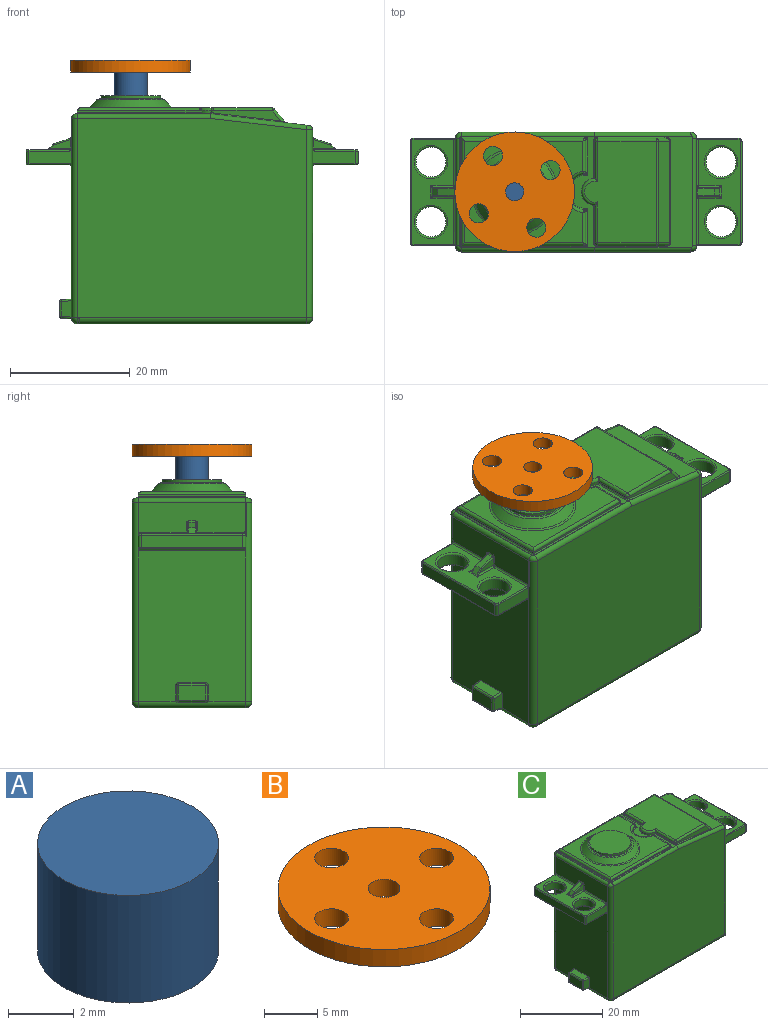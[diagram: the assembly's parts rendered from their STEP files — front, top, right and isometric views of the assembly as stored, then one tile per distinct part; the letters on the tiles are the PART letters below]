
ASSEMBLY  parts=3 mates=4
PART A: 3 faces, bbox 5.5x5.5x4 mm
  f0: cylinder r=2.75mm len=5.5mm, axis (0,0,1), area 69.1mm2, adj f1,f2
  f1: plane 5.5x5.5mm, normal (0,0,-1), area 23.8mm2, adj f0
  f2: plane 5.5x5.5mm, normal (0,0,1), area 23.8mm2, adj f0
PART B: 8 faces, bbox 20x20x2 mm
  f0: cylinder r=1.5mm len=3mm, axis (0,0,-1), area 18.8mm2, adj f2,f3
  f1: cylinder r=10mm len=20mm, axis (0,0,-1), area 125.7mm2, adj f2,f3
  f2: plane 20x20mm, normal (0,0,1), area 274.9mm2, adj f0,f1,f4,f5,f6,f7
  f3: plane 20x20mm, normal (0,0,-1), area 274.9mm2, adj f0,f1,f4,f5,f6,f7
  f4: cylinder r=1.6mm len=3.2mm, axis (0,0,1), area 20.1mm2, adj f2,f3
  f5: cylinder r=1.6mm len=3.2mm, axis (0,0,1), area 20.1mm2, adj f2,f3
  f6: cylinder r=1.6mm len=3.2mm, axis (0,0,1), area 20.1mm2, adj f2,f3
  f7: cylinder r=1.6mm len=3.2mm, axis (0,0,1), area 20.1mm2, adj f2,f3
PART C: 234 faces, bbox 55.8x20.2x38.3 mm
  f0: torus R=2.8mm, axis (0,0,1), area 7.7mm2, adj f17,f31
  f1: torus R=2.8mm, axis (0,0,1), area 7.7mm2, adj f18,f31
  f2: torus R=2.8mm, axis (0,0,1), area 7.7mm2, adj f18,f21
  f3: torus R=2.8mm, axis (0,0,1), area 7.7mm2, adj f17,f21
  f4: torus R=2.8mm, axis (0,0,1), area 7.7mm2, adj f15,f22
  f5: torus R=2.8mm, axis (0,0,1), area 7.7mm2, adj f16,f22
  f6: torus R=2.8mm, axis (0,0,1), area 7.7mm2, adj f16,f20
  f7: torus R=2.8mm, axis (0,0,1), area 7.7mm2, adj f15,f20
  f8: torus R=7.21mm, axis (0,0,1), area 17.3mm2, adj f11,f114
  f9: torus R=5.29mm, axis (0,0,-1), area 13.5mm2, adj f11,f121
  f10: cylinder r=5mm len=10mm, axis (0,0,1), area 15.7mm2, adj f121,f122
  f11: cone r=5.5mm half-angle=45deg, axis (0,0,-1), area 67mm2, adj f8,f9
  f12: cylinder r=2.25mm len=4.5mm, axis (0,0,-1), area 3.5mm2, adj f66,f89,f90,f105,f196,f205
  f13: cylinder r=1mm len=33.35mm, axis (0,0,-1), area 52.4mm2, adj f23,f30,f39,f48,f67,f77,f165,f173
  f14: cylinder r=1mm len=33.35mm, axis (0,0,-1), area 52.5mm2, adj f25,f26,f39,f47,f67,f73,f159,f179
  f15: cylinder r=2.5mm len=5mm, axis (0,0,-1), area 29.8mm2, adj f4,f7
  f16: cylinder r=2.5mm len=5mm, axis (0,0,-1), area 29.8mm2, adj f5,f6
  f17: cylinder r=2.5mm len=5mm, axis (0,0,-1), area 29.8mm2, adj f0,f3
  f18: cylinder r=2.5mm len=5mm, axis (0,0,-1), area 29.8mm2, adj f1,f2
  f19: plane 18.3x0.05mm, normal (0,0,1), area 0.9mm2, adj f73,f75,f77,f131
  f20: plane 17.6x7.1mm, normal (0,0,1), area 67.6mm2, adj f6,f7,f154,f155,f156,f157,f158,f160
  f21: plane 17.6x7.1mm, normal (0,0,-1), area 75.7mm2, adj f2,f3,f145,f167,f168,f170,f171,f172
  f22: plane 17.6x7.1mm, normal (0,0,-1), area 75.7mm2, adj f4,f5,f152,f174,f175,f176,f177,f178
  f23: plane 7.1x2.3mm, normal (0,-1,0), area 14.9mm2, adj f13,f35,f164,f165,f173,f174
  f24: plane 17x2.1mm, normal (-1,0,0), area 35.7mm2, adj f34,f35,f162,f176
  f25: plane 7.1x2.3mm, normal (0,1,0), area 14.9mm2, adj f14,f34,f159,f160,f178,f179
  f26: plane 38.3x33.35mm, normal (0,1,0), area 1262.2mm2, adj f14,f33,f43,f70,f71
  f27: plane 7.1x2.3mm, normal (0,1,0), area 14.9mm2, adj f33,f36,f166,f167,f185,f186
  f28: plane 17x2.1mm, normal (1,0,0), area 35.7mm2, adj f36,f37,f170,f183
  f29: plane 7.1x2.3mm, normal (0,-1,0), area 14.9mm2, adj f32,f37,f169,f171,f180,f181
  f30: plane 38.3x33.35mm, normal (0,-1,0), area 1262.2mm2, adj f13,f32,f42,f78,f79
  f31: plane 17.6x7.1mm, normal (0,0,1), area 67.6mm2, adj f0,f1,f147,f148,f149,f150,f151,f181
  f32: cylinder r=1mm len=31.46mm, axis (0,0,-1), area 49.5mm2, adj f29,f30,f38,f45,f68,f76,f169,f180
  f33: cylinder r=1mm len=31.46mm, axis (0,0,-1), area 49.5mm2, adj f26,f27,f38,f46,f68,f72,f166,f186
  f34: cylinder r=0.5mm len=2.1mm, axis (0,0,-1), area 1.6mm2, adj f24,f25,f161,f177
  f35: cylinder r=0.5mm len=2.1mm, axis (0,0,-1), area 1.6mm2, adj f23,f24,f163,f175
  f36: cylinder r=0.5mm len=2.1mm, axis (0,0,-1), area 1.6mm2, adj f27,f28,f168,f184
  f37: cylinder r=0.5mm len=2.1mm, axis (0,0,-1), area 1.6mm2, adj f28,f29,f172,f182
  f38: plane 25.38x18.08mm, normal (1,0,0), area 455.3mm2, adj f32,f33,f41,f145,f166,f169
  f39: plane 25.38x18.08mm, normal (-1,0,0), area 438.4mm2, adj f13,f14,f44,f50,f52,f53,f54,f55
  f40: plane 38.3x18mm, normal (0,0,-1), area 689.4mm2, adj f41,f42,f43,f44
  f41: cylinder r=1mm len=18mm, axis (0,-1,0), area 28.3mm2, adj f38,f40,f45,f46
  f42: cylinder r=1mm len=38.3mm, axis (-1,0,0), area 60.2mm2, adj f30,f40,f45,f48
  f43: cylinder r=1mm len=38.3mm, axis (1,0,0), area 60.2mm2, adj f26,f40,f46,f47
  f44: cylinder r=1mm len=18mm, axis (0,1,0), area 27.4mm2, adj f39,f40,f47,f48,f51,f60,f61
  f45: sphere r=1mm, area 1.6mm2, adj f32,f41,f42
  f46: sphere r=1mm, area 1mm2, adj f33,f41,f43
  f47: sphere r=1mm, area 1.6mm2, adj f14,f43,f44
  f48: sphere r=1mm, area 2.1mm2, adj f13,f42,f44
  f49: plane 4.45x2.45mm, normal (-1,0,0), area 10.9mm2, adj f56,f59,f62,f65
  f50: plane 2.75x1.73mm, normal (-0.09,1,0), area 4.5mm2, adj f39,f55,f61,f62
  f51: plane 4.76x1.74mm, normal (-0.09,0,-1), area 8mm2, adj f44,f60,f61,f65
  f52: plane 2.75x1.73mm, normal (-0.09,-1,0), area 4.5mm2, adj f39,f54,f59,f60
  f53: plane 4.75x1.73mm, normal (-0.09,0,1), area 8mm2, adj f39,f54,f55,f56
  f54: cylinder r=0.3mm len=1.74mm, axis (0.99,-0.09,0.09), area 0.8mm2, adj f39,f52,f53,f57
  f55: cylinder r=0.3mm len=1.74mm, axis (0.99,0.09,0.09), area 0.8mm2, adj f39,f50,f53,f58
  f56: cylinder r=0.3mm len=4.45mm, axis (0,-1,0), area 2mm2, adj f49,f53,f57,f58
  f57: sphere r=0.3mm, area 0.1mm2, adj f54,f56,f59
  f58: sphere r=0.3mm, area 0.1mm2, adj f55,f56,f62
  f59: cylinder r=0.3mm len=2.45mm, axis (0,0,-1), area 1.1mm2, adj f49,f52,f57,f63
  f60: cylinder r=0.3mm len=1.75mm, axis (0.99,-0.09,-0.09), area 0.8mm2, adj f39,f44,f51,f52,f63
  f61: cylinder r=0.3mm len=1.75mm, axis (0.99,0.09,-0.09), area 0.8mm2, adj f39,f44,f50,f51,f64
  f62: cylinder r=0.3mm len=2.45mm, axis (0,0,1), area 1.1mm2, adj f49,f50,f58,f64
  f63: sphere r=0.3mm, area 0.1mm2, adj f59,f60,f65
  f64: sphere r=0.3mm, area 0.1mm2, adj f61,f62,f65
  f65: cylinder r=0.3mm len=4.45mm, axis (0,1,0), area 2mm2, adj f49,f51,f63,f64
  f66: plane 22.46x18.5mm, normal (0,0,1), area 29mm2, adj f12,f69,f71,f73,f77,f79,f123,f125
  f67: plane 18.2x5.15mm, normal (-1,0,0), area 85.5mm2, adj f13,f14,f75,f153,f154,f156,f159,f165
  f68: plane 18.2x3.23mm, normal (1,0,0), area 51mm2, adj f32,f33,f74,f146,f147,f149,f180,f186
  f69: plane 18.53x16.37mm, normal (0.12,0,0.99), area 70.4mm2, adj f66,f70,f72,f74,f76,f78,f198,f199
  f70: cylinder r=0.75mm len=16.18mm, axis (0.99,0,-0.12), area 19.1mm2, adj f26,f69,f71,f72
  f71: cylinder r=0.75mm len=22.3mm, axis (-1,0,0), area 26.2mm2, adj f26,f66,f70,f73
  f72: bspline ~1x1mm, area 1.3mm2, adj f33,f69,f70,f74
  f73: torus R=0.25mm, axis (0,0,1), area 1.3mm2, adj f14,f19,f66,f71,f75,f124,f127
  f74: cylinder r=0.75mm len=18mm, axis (0,1,0), area 19.6mm2, adj f68,f69,f72,f76
  f75: cylinder r=0.75mm len=18mm, axis (0,-1,0), area 21.2mm2, adj f19,f67,f73,f77
  f76: bspline ~1x1mm, area 1.3mm2, adj f32,f69,f74,f78
  f77: torus R=0.25mm, axis (0,0,1), area 1.3mm2, adj f13,f19,f66,f75,f79,f130,f132
  f78: cylinder r=0.75mm len=16.18mm, axis (-0.99,0,0.12), area 19.1mm2, adj f30,f69,f76,f79
  f79: cylinder r=0.75mm len=22.3mm, axis (1,0,0), area 26.2mm2, adj f30,f66,f77,f78
  f80: plane 2.8x1.1mm, normal (-0.32,0,0.95), area 3.2mm2, adj f83,f153,f220,f230
  f81: plane 3.22x1.42mm, normal (0,-1,0), area 2.8mm2, adj f155,f218,f220,f223
  f82: plane 3.22x1.42mm, normal (0,1,0), area 2.8mm2, adj f158,f228,f230,f232
  f83: plane 1.4x0.92mm, normal (-0.71,0,0.71), area 1.5mm2, adj f80,f157,f217,f218,f226,f228
  f84: plane 2.8x1.1mm, normal (0.32,0,0.95), area 3.2mm2, adj f87,f146,f191,f212
  f85: plane 3.22x1.42mm, normal (0,-1,0), area 2.8mm2, adj f148,f210,f212,f214
  f86: plane 3.22x1.42mm, normal (0,1,0), area 2.8mm2, adj f151,f189,f191,f194
  f87: plane 1.4x0.92mm, normal (0.71,0,0.71), area 1.5mm2, adj f84,f150,f188,f189,f208,f210
  f88: plane 11.16x1.67mm, normal (0,1,0), area 10.1mm2, adj f94,f95,f101,f203
  f89: plane 6.25x0.3mm, normal (-1,0,0), area 1.9mm2, adj f12,f95,f104,f205
  f90: plane 6.25x0.3mm, normal (-1,0,0), area 1.9mm2, adj f12,f96,f106,f196
  f91: plane 11.16x1.67mm, normal (0,-1,0), area 10.1mm2, adj f93,f96,f98,f199
  f92: plane 17x2.24mm, normal (0.77,0,0.64), area 49.5mm2, adj f93,f94,f100,f201
  f93: cylinder r=0.5mm len=2.56mm, axis (0.64,0,-0.77), area 2mm2, adj f91,f92,f99,f200
  f94: cylinder r=0.5mm len=2.56mm, axis (-0.64,0,0.77), area 2mm2, adj f88,f92,f102,f202
  f95: cylinder r=0.5mm len=0.5mm, axis (0,0,-1), area 0.2mm2, adj f88,f89,f103,f204,f206
  f96: cylinder r=0.5mm len=0.5mm, axis (0,0,-1), area 0.2mm2, adj f90,f91,f107,f197,f198
  f97: plane 17x12.02mm, normal (0,0,1), area 172.6mm2, adj f98,f100,f101,f104,f105,f106
  f98: cylinder r=0.5mm len=9.77mm, axis (-1,0,0), area 7.7mm2, adj f91,f97,f99,f107
  f99: sphere r=0.5mm, area 0.2mm2, adj f93,f98,f100
  f100: cylinder r=0.5mm len=17mm, axis (0,1,0), area 7.4mm2, adj f92,f97,f99,f102
  f101: cylinder r=0.5mm len=9.77mm, axis (1,0,0), area 7.7mm2, adj f88,f97,f102,f103
  f102: sphere r=0.5mm, area 0.2mm2, adj f94,f100,f101
  f103: sphere r=0.5mm, area 0.2mm2, adj f95,f101,f104
  f104: cylinder r=0.5mm len=6.82mm, axis (0,1,0), area 5.1mm2, adj f89,f97,f103,f105
  f105: torus R=1.75mm, axis (0,0,1), area 5.6mm2, adj f12,f97,f104,f106
  f106: cylinder r=0.5mm len=6.82mm, axis (0,1,0), area 5.1mm2, adj f90,f97,f105,f107
  f107: sphere r=0.5mm, area 0.4mm2, adj f96,f98,f106
  f108: plane 20.5x0.3mm, normal (0,-1,0), area 6.2mm2, adj f109,f117,f129,f134
  f109: plane 18x0.3mm, normal (-1,0,0), area 5.4mm2, adj f108,f110,f115,f131
  f110: plane 20.5x0.3mm, normal (0,1,0), area 6.2mm2, adj f109,f116,f128,f137
  f111: plane 5.41x0.3mm, normal (1,0,0), area 1.6mm2, adj f118,f125,f137,f144
  f112: cylinder r=3mm len=5.98mm, axis (0,0,1), area 2.7mm2, adj f120,f123,f141,f144
  f113: plane 5.41x0.3mm, normal (1,0,0), area 1.6mm2, adj f119,f126,f134,f141
  f114: plane 19.8x17mm, normal (0,0,1), area 157.7mm2, adj f8,f115,f116,f117,f118,f119,f120
  f115: cylinder r=0.5mm len=18mm, axis (0,-1,0), area 13.7mm2, adj f109,f114,f116,f117
  f116: cylinder r=0.5mm len=20.5mm, axis (-1,0,0), area 15.8mm2, adj f110,f114,f115,f138
  f117: cylinder r=0.5mm len=20.5mm, axis (1,0,0), area 15.8mm2, adj f108,f114,f115,f133
  f118: cylinder r=0.5mm len=5.41mm, axis (0,1,0), area 4.1mm2, adj f111,f114,f138,f143
  f119: cylinder r=0.5mm len=5.41mm, axis (0,1,0), area 4.1mm2, adj f113,f114,f133,f140
  f120: torus R=3.5mm, axis (0,0,1), area 7.3mm2, adj f112,f114,f140,f143
  f121: plane 10.59x10.59mm, normal (0,0,1), area 9.5mm2, adj f9,f10
  f122: plane 10x10mm, normal (0,0,1), area 78.5mm2, adj f10
  f123: torus R=2.8mm, axis (0,0,1), area 2.9mm2, adj f66,f112,f139,f142
  f124: cylinder r=0.18mm len=0.05mm, axis (1,-0.09,0.02), area 0mm2, adj f73,f127,f128
  f125: cylinder r=0.2mm len=6.41mm, axis (0,-1,0), area 1.9mm2, adj f66,f111,f136,f142
  f126: cylinder r=0.2mm len=6.41mm, axis (0,-1,0), area 1.9mm2, adj f66,f113,f135,f139
  f127: cylinder r=0.18mm len=0.05mm, axis (-0.08,-1,0), area 0mm2, adj f73,f124,f131
  f128: cylinder r=0.2mm len=21.15mm, axis (1,0,0), area 6.5mm2, adj f66,f110,f124,f131,f136
  f129: cylinder r=0.2mm len=21.15mm, axis (-1,0,0), area 6.5mm2, adj f66,f108,f130,f131,f135
  f130: cylinder r=0.18mm len=0.05mm, axis (1,-0.08,0), area 0mm2, adj f77,f129,f132
  f131: cylinder r=0.2mm len=18.3mm, axis (0,1,0), area 5.7mm2, adj f19,f109,f127,f128,f129,f132
  f132: cylinder r=0.18mm len=0.05mm, axis (0.09,1,0.02), area 0mm2, adj f77,f130,f131
  f133: bspline ~0.5x0.5mm, area 0.2mm2, adj f117,f119,f134
  f134: cylinder r=0.3mm len=0.3mm, axis (0,0,1), area 0.1mm2, adj f108,f113,f133,f135
  f135: bspline ~0.5x0.5mm, area 0.1mm2, adj f126,f129,f134
  f136: bspline ~0.5x0.5mm, area 0.1mm2, adj f125,f128,f137
  f137: cylinder r=0.3mm len=0.3mm, axis (0,0,1), area 0.1mm2, adj f110,f111,f136,f138
  f138: bspline ~0.5x0.5mm, area 0.2mm2, adj f116,f118,f137
  f139: bspline ~0.49x0.47mm, area 0.1mm2, adj f123,f126,f141
  f140: bspline ~0.5x0.5mm, area 0.2mm2, adj f119,f120,f141
  f141: cylinder r=0.3mm len=0.3mm, axis (0,0,1), area 0.1mm2, adj f112,f113,f139,f140
  f142: bspline ~0.49x0.47mm, area 0.1mm2, adj f123,f125,f144
  f143: bspline ~0.5x0.5mm, area 0.2mm2, adj f118,f120,f144
  f144: cylinder r=0.3mm len=0.3mm, axis (0,0,1), area 0.1mm2, adj f111,f112,f142,f143
  f145: cylinder r=0.3mm len=17.6mm, axis (0,-1,0), area 8.3mm2, adj f21,f38,f166,f169
  f146: cylinder r=0.3mm len=1.1mm, axis (0,1,0), area 0.4mm2, adj f68,f84,f190,f209
  f147: cylinder r=0.3mm len=7.85mm, axis (0,-1,0), area 3.7mm2, adj f31,f68,f180,f215
  f148: cylinder r=0.3mm len=3.92mm, axis (-1,0,0), area 1.7mm2, adj f31,f85,f207,f208,f215
  f149: cylinder r=0.3mm len=7.85mm, axis (0,-1,0), area 3.7mm2, adj f31,f68,f186,f195
  f150: cylinder r=0.3mm len=2.1mm, axis (0,1,0), area 0.4mm2, adj f31,f87,f187,f207
  f151: cylinder r=0.3mm len=3.92mm, axis (1,0,0), area 1.7mm2, adj f31,f86,f187,f188,f195
  f152: cylinder r=0.3mm len=17.6mm, axis (0,1,0), area 8.3mm2, adj f22,f39,f173,f179
  f153: cylinder r=0.3mm len=1.1mm, axis (0,-1,0), area 0.4mm2, adj f67,f80,f219,f227
  f154: cylinder r=0.3mm len=7.85mm, axis (0,1,0), area 3.7mm2, adj f20,f67,f165,f224
  f155: cylinder r=0.3mm len=3.92mm, axis (-1,0,0), area 1.7mm2, adj f20,f81,f216,f217,f224
  f156: cylinder r=0.3mm len=7.85mm, axis (0,1,0), area 3.7mm2, adj f20,f67,f159,f233
  f157: cylinder r=0.3mm len=2.1mm, axis (0,1,0), area 0.4mm2, adj f20,f83,f216,f225
  f158: cylinder r=0.3mm len=3.92mm, axis (1,0,0), area 1.7mm2, adj f20,f82,f225,f226,f233
  f159: torus R=0.5mm, axis (0,1,0), area 0.1mm2, adj f14,f25,f67,f156,f160
  f160: cylinder r=0.2mm len=6.8mm, axis (1,0,0), area 2.1mm2, adj f20,f25,f159,f161
  f161: torus R=0.3mm, axis (0,0,1), area 0.2mm2, adj f20,f34,f160,f162
  f162: cylinder r=0.2mm len=17mm, axis (0,1,0), area 5.3mm2, adj f20,f24,f161,f163
  f163: torus R=0.3mm, axis (0,0,1), area 0.2mm2, adj f20,f35,f162,f164
  f164: cylinder r=0.2mm len=6.8mm, axis (-1,0,0), area 2.1mm2, adj f20,f23,f163,f165
  f165: torus R=0.5mm, axis (0,-1,0), area 0.1mm2, adj f13,f23,f67,f154,f164
  f166: torus R=0.5mm, axis (0,1,0), area 0.1mm2, adj f27,f33,f38,f145,f167
  f167: cylinder r=0.2mm len=6.8mm, axis (-1,0,0), area 2.1mm2, adj f21,f27,f166,f168
  f168: torus R=0.3mm, axis (0,0,1), area 0.2mm2, adj f21,f36,f167,f170
  f169: torus R=0.5mm, axis (0,-1,0), area 0.1mm2, adj f29,f32,f38,f145,f171
  f170: cylinder r=0.2mm len=17mm, axis (0,1,0), area 5.3mm2, adj f21,f28,f168,f172
  f171: cylinder r=0.2mm len=6.8mm, axis (1,0,0), area 2.1mm2, adj f21,f29,f169,f172
  f172: torus R=0.3mm, axis (0,0,1), area 0.2mm2, adj f21,f37,f170,f171
  f173: torus R=0.5mm, axis (0,-1,0), area 0.1mm2, adj f13,f23,f39,f152,f174
  f174: cylinder r=0.2mm len=6.8mm, axis (1,0,0), area 2.1mm2, adj f22,f23,f173,f175
  f175: torus R=0.3mm, axis (0,0,1), area 0.2mm2, adj f22,f35,f174,f176
  f176: cylinder r=0.2mm len=17mm, axis (0,-1,0), area 5.3mm2, adj f22,f24,f175,f177
  f177: torus R=0.3mm, axis (0,0,1), area 0.2mm2, adj f22,f34,f176,f178
  f178: cylinder r=0.2mm len=6.8mm, axis (-1,0,0), area 2.1mm2, adj f22,f25,f177,f179
  f179: torus R=0.5mm, axis (0,1,0), area 0.1mm2, adj f14,f25,f39,f152,f178
  f180: torus R=0.5mm, axis (0,-1,0), area 0.1mm2, adj f29,f32,f68,f147,f181
  f181: cylinder r=0.2mm len=6.8mm, axis (-1,0,0), area 2.1mm2, adj f29,f31,f180,f182
  f182: torus R=0.3mm, axis (0,0,1), area 0.2mm2, adj f31,f37,f181,f183
  f183: cylinder r=0.2mm len=17mm, axis (0,-1,0), area 5.3mm2, adj f28,f31,f182,f184
  f184: torus R=0.3mm, axis (0,0,1), area 0.2mm2, adj f31,f36,f183,f185
  f185: cylinder r=0.2mm len=6.8mm, axis (1,0,0), area 2.1mm2, adj f27,f31,f184,f186
  f186: torus R=0.5mm, axis (0,1,0), area 0.1mm2, adj f27,f33,f68,f149,f185
  f187: bspline ~0.35x0.35mm, area 0mm2, adj f150,f151,f188
  f188: bspline ~0.5x0.35mm, area 0.1mm2, adj f87,f151,f187,f189
  f189: cylinder r=0.2mm len=0.7mm, axis (-0.71,0,0.71), area 0.2mm2, adj f86,f87,f188,f191
  f190: torus R=0.5mm, axis (0,-1,0), area 0mm2, adj f146,f191,f192
  f191: cylinder r=0.2mm len=2.86mm, axis (-0.95,0,0.32), area 0.9mm2, adj f84,f86,f189,f190,f193
  f192: bspline ~0.39x0.36mm, area 0mm2, adj f68,f190,f193
  f193: bspline ~0.22x0.2mm, area 0mm2, adj f68,f191,f192,f194
  f194: cylinder r=0.2mm len=1.42mm, axis (0,0,-1), area 0.4mm2, adj f68,f86,f193,f195
  f195: bspline ~0.3x0.3mm, area 0.1mm2, adj f149,f151,f194
  f196: cylinder r=0.2mm len=6.26mm, axis (0,-1,0), area 2mm2, adj f12,f66,f90,f197
  f197: torus R=0.7mm, axis (0,0,1), area 0.1mm2, adj f66,f96,f196,f198
  f198: bspline ~0.51x0.34mm, area 0.1mm2, adj f66,f69,f96,f197,f199
  f199: cylinder r=0.2mm len=11.18mm, axis (-0.99,0,0.12), area 3.5mm2, adj f69,f91,f198,f200
  f200: bspline ~1.01x0.7mm, area 0.3mm2, adj f69,f93,f199,f201
  f201: cylinder r=0.2mm len=17mm, axis (0,-1,0), area 2.6mm2, adj f69,f92,f200,f202
  f202: bspline ~1.01x0.7mm, area 0.3mm2, adj f69,f94,f201,f203
  f203: cylinder r=0.2mm len=11.18mm, axis (0.99,0,-0.12), area 3.5mm2, adj f69,f88,f202,f204
  f204: bspline ~0.51x0.34mm, area 0.1mm2, adj f66,f69,f95,f203,f206
  f205: cylinder r=0.2mm len=6.26mm, axis (0,-1,0), area 2mm2, adj f12,f66,f89,f206
  f206: torus R=0.7mm, axis (0,0,1), area 0.1mm2, adj f66,f95,f204,f205
  f207: bspline ~0.35x0.35mm, area 0mm2, adj f148,f150,f208
  f208: bspline ~0.5x0.35mm, area 0.1mm2, adj f87,f148,f207,f210
  f209: torus R=0.5mm, axis (0,-1,0), area 0mm2, adj f146,f211,f212
  f210: cylinder r=0.2mm len=0.7mm, axis (0.71,0,-0.71), area 0.2mm2, adj f85,f87,f208,f212
  f211: bspline ~0.39x0.36mm, area 0mm2, adj f68,f209,f213
  f212: cylinder r=0.2mm len=2.86mm, axis (0.95,0,-0.32), area 0.9mm2, adj f84,f85,f209,f210,f213
  f213: bspline ~0.22x0.2mm, area 0mm2, adj f68,f211,f212,f214
  f214: cylinder r=0.2mm len=1.42mm, axis (0,0,1), area 0.4mm2, adj f68,f85,f213,f215
  f215: bspline ~0.3x0.3mm, area 0.1mm2, adj f147,f148,f214
  f216: bspline ~0.35x0.35mm, area 0mm2, adj f155,f157,f217
  f217: bspline ~0.5x0.35mm, area 0.1mm2, adj f83,f155,f216,f218
  f218: cylinder r=0.2mm len=0.7mm, axis (-0.71,0,-0.71), area 0.2mm2, adj f81,f83,f217,f220
  f219: torus R=0.5mm, axis (0,1,0), area 0mm2, adj f153,f220,f221
  f220: cylinder r=0.2mm len=2.86mm, axis (-0.95,0,-0.32), area 0.9mm2, adj f80,f81,f218,f219,f222
  f221: bspline ~0.39x0.36mm, area 0mm2, adj f67,f219,f222
  f222: bspline ~0.22x0.2mm, area 0mm2, adj f67,f220,f221,f223
  f223: cylinder r=0.2mm len=1.42mm, axis (0,0,-1), area 0.4mm2, adj f67,f81,f222,f224
  f224: bspline ~0.3x0.3mm, area 0.1mm2, adj f154,f155,f223
  f225: bspline ~0.35x0.35mm, area 0mm2, adj f157,f158,f226
  f226: bspline ~0.5x0.35mm, area 0.1mm2, adj f83,f158,f225,f228
  f227: torus R=0.5mm, axis (0,1,0), area 0mm2, adj f153,f229,f230
  f228: cylinder r=0.2mm len=0.7mm, axis (0.71,0,0.71), area 0.2mm2, adj f82,f83,f226,f230
  f229: bspline ~0.39x0.36mm, area 0mm2, adj f67,f227,f231
  f230: cylinder r=0.2mm len=2.86mm, axis (0.95,0,0.32), area 0.9mm2, adj f80,f82,f227,f228,f231
  f231: bspline ~0.22x0.2mm, area 0mm2, adj f67,f229,f230,f232
  f232: cylinder r=0.2mm len=1.42mm, axis (0,0,1), area 0.4mm2, adj f67,f82,f231,f233
  f233: bspline ~0.3x0.3mm, area 0.1mm2, adj f156,f158,f232
PLACE A rot(axis=(0,0,1),0deg) t=(-30.93,7.56,-1.19)mm
PLACE B rot(axis=(0,0,-1),58.8deg) t=(-41.18,7.56,40.91)mm
PLACE C t=(-30.93,7.56,-1.19)mm fixed
MATE cylindrical A.f0 <-> B.f1  axis (0,0,1) through (-41.18,7.56,40.91)mm
MATE revolute A.f0 <-> C.f10  axis (0,0,-1) through (-41.18,7.56,36.91)mm
MATE revolute A.f0 <-> B.f1  axis (0,0,1) through (-41.18,7.56,40.91)mm
MATE cylindrical C.f10 <-> A.f0  axis (0,0,1) through (-41.18,7.56,36.91)mm
